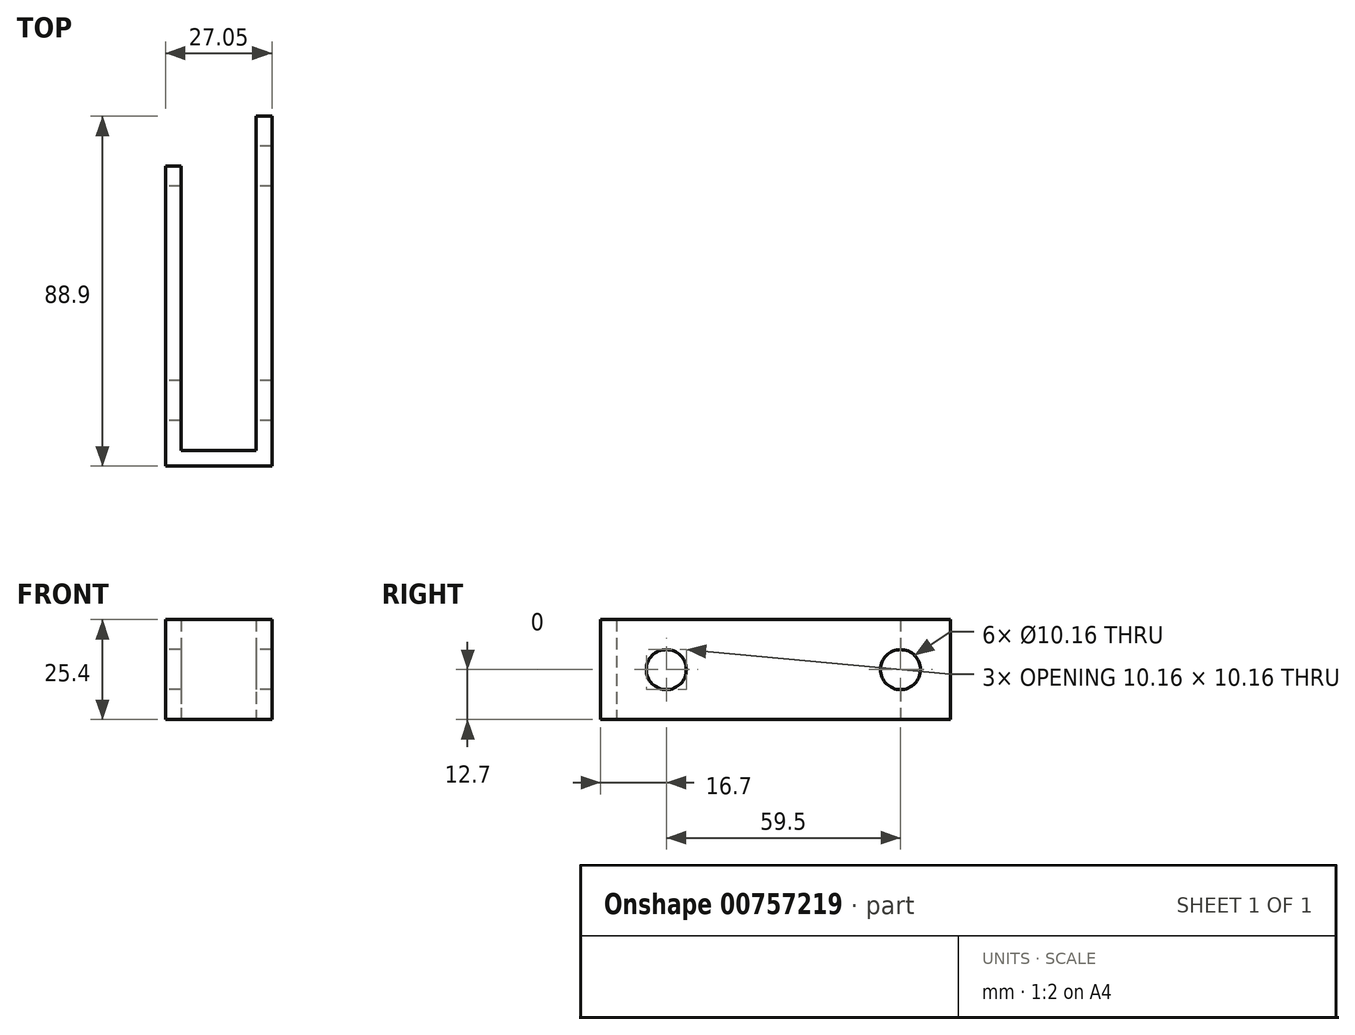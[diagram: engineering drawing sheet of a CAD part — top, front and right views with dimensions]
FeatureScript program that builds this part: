
annotation { "Feature Type Name" : "Feature", "Feature Type Description" : "" }
export const myFeature = defineFeature(function(context is Context, id is Id, definition is map)
    precondition{}
    {
        {
            var Q0;
            Q0=qCreatedBy(makeId("Top.planeOp"),FACE);
            var sketch = newSketch(context, id + "F0", { "sketchPlane" : qUnion([Q0])});
            skLineSegment(sketch, "E0", {"start": v(0, 0) * mm, "end": v(0, 76.2) * mm});
            skLineSegment(sketch, "E1", {"start": v(0, 76.2) * mm, "end": v(4, 76.2) * mm});
            skLineSegment(sketch, "E2", {"start": v(4, 76.2) * mm, "end": v(4, 4) * mm});
            skLineSegment(sketch, "E3", {"start": v(0, 0) * mm, "end": v(27.05, 0) * mm});
            skLineSegment(sketch, "E4", {"start": v(4, 4) * mm, "end": v(23.05, 4) * mm});
            skLineSegment(sketch, "E5", {"start": v(23.05, 4) * mm, "end": v(23.05, 88.9) * mm});
            skLineSegment(sketch, "E6", {"start": v(23.05, 88.9) * mm, "end": v(27.05, 88.9) * mm});
            skLineSegment(sketch, "E7", {"start": v(27.05, 88.9) * mm, "end": v(27.05, 0) * mm});
            skSolve(sketch);
        }
        {
            var Q0;
            Q0 = qSketchRegion(id + "F0", true);
            extrude(context, id + "F1", {"entities" : qUnion([Q0]), "depth" : 25.4 * mm, "offsetDistance" : 25.4 * mm});
        }
        {
            var Q0;
            Q0=makeQuery(id+"F1.opExtrude","SWEPT_FACE",FACE,{"disambiguationData":[OSD([sQuery(id+"F0.wireOp",EDGE,"E5")])]});
            var sketch = newSketch(context, id + "F2", { "sketchPlane" : qUnion([Q0])});
            skCircle(sketch, "E8", {"center": v(-76.2, 12.7) * mm, "radius": 5.08 * mm});
            skPoint(sketch, "E8.centerSnap0", {"position": v(-88.9, 12.7) * mm});
            skCircle(sketch, "E9", {"center": v(-16.7, 12.7) * mm, "radius": 5.08 * mm});
            skSolve(sketch);
        }
        {
            var Q0;
            Q0 = qSketchRegion(id + "F2", true);
            extrude(context, id + "F3", {"entities" : qUnion([Q0]), "operationType" : NewBodyOperationType.REMOVE, "endBound" : BoundingType.SYMMETRIC, "oppositeDirection" : true, "depth" : 152.4 * mm, "offsetDistance" : 25.4 * mm});
        }
    });
